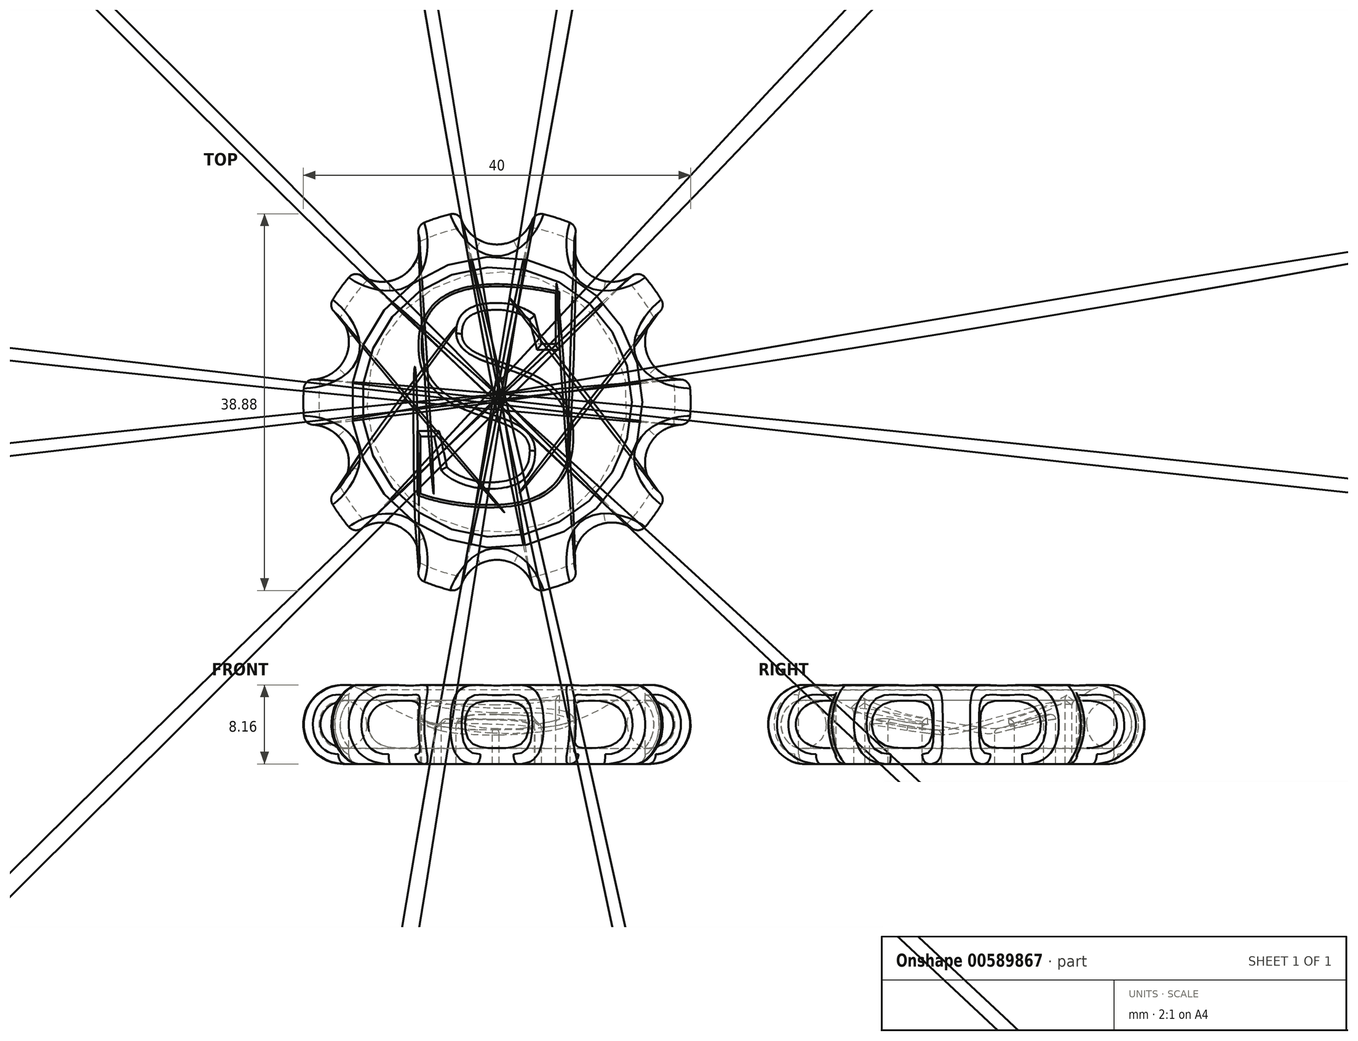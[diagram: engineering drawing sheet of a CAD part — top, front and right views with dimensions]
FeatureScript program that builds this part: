
annotation { "Feature Type Name" : "Feature", "Feature Type Description" : "" }
export const myFeature = defineFeature(function(context is Context, id is Id, definition is map)
    precondition{}
    {
        {
            var Q0;
            Q0=qCreatedBy(makeId("Right.planeOp"),FACE);
            var sketch = newSketch(context, id + "F0", { "sketchPlane" : qUnion([Q0])});
            skArc(sketch, "E0", {"start": v(-13.4, 7.3) * mm, "mid": v(-19.78, 5.4) * mm, "end": v(-15.92, 0) * mm});
            skLineSegment(sketch, "E1", {"start": v(0, 0) * mm, "end": v(-15.92, 0) * mm});
            skLineSegment(sketch, "E2", {"start": v(0, 0) * mm, "end": v(0, 3.46) * mm});
            skFitSpline(sketch, "E3", {"points": [v(0, 3.46) * mm, v(-7.36, 4.25) * mm, v(-13.95, 7.65) * mm], "startDerivative": vector(-15.17, 0.2) * mm, "endDerivative": vector(-12.72, 8.5) * mm});
            skFitSpline(sketch, "E4", {"points": [v(-13.95, 7.65) * mm, v(-15.03, 8.06) * mm], "startDerivative": vector(-1.09, 0.4) * mm, "endDerivative": vector(-1.09, 0.4) * mm});
            skLineSegment(sketch, "E5", {"start": v(0, 3.46) * mm, "end": v(0, 0) * mm});
            skPoint(sketch, "E6.orphan", {"position": v(0, 6.33) * mm});
            skCircle(sketch, "E7", {"center": v(-15.92, 4.08) * mm, "radius": 2.48 * mm});
            skSolve(sketch);
        }
        {
            var Q0;
            {var subQ6=sQuery(id+"F0.wireOp",EDGE,"E1");Q0=makeQuery(id+"F0.imprint","IMPRINT",FACE,{"disambiguationData":[TD([[makeQuery(id+"F0.imprint","IMPRINT",EDGE,{"derivedFrom":subQ6}),-1.0]])]});}
            var Q1;
            Q1=sQuery(id+"F0.wireOp",EDGE,"E5");
            revolve(context, id + "F1", {"entities" : qUnion([Q0]), "axis" : qUnion([Q1]), "revolveType" : RevolveType.FULL});
        }
        {
            var Q0;
            Q0=makeQuery(id+"F0.imprint","IMPRINT",FACE,{"disambiguationData":[TD([[makeQuery(id+"F0.imprint","IMPRINT",EDGE,{"derivedFrom":sQuery(id+"F0.wireOp",EDGE,"E7")}),1.0]])]});
            var Q1;
            Q1=sQuery(id+"F0.wireOp",EDGE,"E5");
            revolve(context, id + "F2", {"entities" : qUnion([Q0]), "axis" : qUnion([Q1]), "revolveType" : RevolveType.FULL});
        }
        {
            var Q0;
            Q0=qCreatedBy(makeId("Top.planeOp"),FACE);
            cPlane(context, id + "F3", {"entities" : qUnion([Q0]), "cplaneType" : CPlaneType.OFFSET, "offset" : 12 * mm, "width" : 150 * mm, "height" : 150 * mm});
        }
        {
            var Q0;
            Q0=qCreatedBy(id+"F3.planeOp",FACE);
            var sketch = newSketch(context, id + "F4", { "sketchPlane" : qUnion([Q0])});
            skText(sketch, "E8", { "text": "S", "fontName": "Tinos-Bold.ttf"});
            const initialGuessF4  = {"E8": [-0.0097, -0.01028, 1, 0, 0.02417]};
            skSetInitialGuess(sketch, initialGuessF4);
            skSolve(sketch);
        }
        {
            var Q0;
            Q0 = qSketchRegion(id + "F4", true);
            extrude(context, id + "F5", {"entities" : qUnion([Q0]), "operationType" : NewBodyOperationType.REMOVE, "oppositeDirection" : true, "depth" : 27.1 * mm, "offsetDistance" : 25 * mm});
        }
        {
            var Q0;
            Q0=qCreatedBy(id+"F3.planeOp",FACE);
            var sketch = newSketch(context, id + "F6", { "sketchPlane" : qUnion([Q0])});
            skCircle(sketch, "E9", {"center": v(0, 20.18) * mm, "radius": 3.9 * mm});
            skCircle(sketch, "E10.1.0", {"center": v(-11.86, 16.33) * mm, "radius": 3.9 * mm});
            skCircle(sketch, "E10.2.0", {"center": v(-19.2, 6.24) * mm, "radius": 3.9 * mm});
            skCircle(sketch, "E10.3.0", {"center": v(-19.2, -6.24) * mm, "radius": 3.9 * mm});
            skCircle(sketch, "E10.4.0", {"center": v(-11.86, -16.33) * mm, "radius": 3.9 * mm});
            skCircle(sketch, "E10.5.0", {"center": v(0, -20.18) * mm, "radius": 3.9 * mm});
            skCircle(sketch, "E10.6.0", {"center": v(11.86, -16.33) * mm, "radius": 3.9 * mm});
            skCircle(sketch, "E10.7.0", {"center": v(19.2, -6.24) * mm, "radius": 3.9 * mm});
            skCircle(sketch, "E10.8.0", {"center": v(19.2, 6.24) * mm, "radius": 3.9 * mm});
            skCircle(sketch, "E10.9.0", {"center": v(11.86, 16.33) * mm, "radius": 3.9 * mm});
            skPoint(sketch, "E10.center", {"position": v(0, 0) * mm});
            skSolve(sketch);
        }
        {
            var Q0;
            Q0 = qSketchRegion(id + "F6", true);
            extrude(context, id + "F7", {"entities" : qUnion([Q0]), "operationType" : NewBodyOperationType.REMOVE, "oppositeDirection" : true, "depth" : 20.8 * mm, "offsetDistance" : 25 * mm});
        }
        {
            var Q0;
            Q0=makeQuery(id+"F7.boolean.opBoolean","INTERSECT",EDGE,{"derivedFrom":[makeQuery(id+"F1.opRevolve","SWEPT_FACE",FACE,{"disambiguationData":[OSD([sQuery(id+"F0.wireOp",EDGE,"E0")])]}),makeQuery(id+"F7.opExtrude","SWEPT_FACE",FACE,{"disambiguationData":[OSD([sQuery(id+"F6.wireOp",EDGE,"E9")])]})]});
            var Q1;
            Q1=makeQuery(id+"F7.boolean.opBoolean","INTERSECT",EDGE,{"derivedFrom":[makeQuery(id+"F1.opRevolve","SWEPT_FACE",FACE,{"disambiguationData":[OSD([sQuery(id+"F0.wireOp",EDGE,"E0")])]}),makeQuery(id+"F7.opExtrude","SWEPT_FACE",FACE,{"disambiguationData":[OSD([sQuery(id+"F6.wireOp",EDGE,"E10.8.0")])]})]});
            var Q2;
            Q2=makeQuery(id+"F7.boolean.opBoolean","INTERSECT",EDGE,{"derivedFrom":[makeQuery(id+"F1.opRevolve","SWEPT_FACE",FACE,{"disambiguationData":[OSD([sQuery(id+"F0.wireOp",EDGE,"E0")])]}),makeQuery(id+"F7.opExtrude","SWEPT_FACE",FACE,{"disambiguationData":[OSD([sQuery(id+"F6.wireOp",EDGE,"E10.9.0")])]})]});
            var Q3;
            Q3=makeQuery(id+"F7.boolean.opBoolean","INTERSECT",EDGE,{"derivedFrom":[makeQuery(id+"F1.opRevolve","SWEPT_FACE",FACE,{"disambiguationData":[OSD([sQuery(id+"F0.wireOp",EDGE,"E0")])]}),makeQuery(id+"F7.opExtrude","SWEPT_FACE",FACE,{"disambiguationData":[OSD([sQuery(id+"F6.wireOp",EDGE,"E10.7.0")])]})]});
            var Q4;
            Q4=makeQuery(id+"F7.boolean.opBoolean","INTERSECT",EDGE,{"derivedFrom":[makeQuery(id+"F1.opRevolve","SWEPT_FACE",FACE,{"disambiguationData":[OSD([sQuery(id+"F0.wireOp",EDGE,"E0")])]}),makeQuery(id+"F7.opExtrude","SWEPT_FACE",FACE,{"disambiguationData":[OSD([sQuery(id+"F6.wireOp",EDGE,"E10.6.0")])]})]});
            var Q5;
            Q5=makeQuery(id+"F7.boolean.opBoolean","INTERSECT",EDGE,{"derivedFrom":[makeQuery(id+"F1.opRevolve","SWEPT_FACE",FACE,{"disambiguationData":[OSD([sQuery(id+"F0.wireOp",EDGE,"E0")])]}),makeQuery(id+"F7.opExtrude","SWEPT_FACE",FACE,{"disambiguationData":[OSD([sQuery(id+"F6.wireOp",EDGE,"E10.5.0")])]})]});
            var Q6;
            Q6=makeQuery(id+"F7.boolean.opBoolean","INTERSECT",EDGE,{"derivedFrom":[makeQuery(id+"F1.opRevolve","SWEPT_FACE",FACE,{"disambiguationData":[OSD([sQuery(id+"F0.wireOp",EDGE,"E0")])]}),makeQuery(id+"F7.opExtrude","SWEPT_FACE",FACE,{"disambiguationData":[OSD([sQuery(id+"F6.wireOp",EDGE,"E10.4.0")])]})]});
            var Q7;
            Q7=makeQuery(id+"F7.boolean.opBoolean","INTERSECT",EDGE,{"derivedFrom":[makeQuery(id+"F1.opRevolve","SWEPT_FACE",FACE,{"disambiguationData":[OSD([sQuery(id+"F0.wireOp",EDGE,"E0")])]}),makeQuery(id+"F7.opExtrude","SWEPT_FACE",FACE,{"disambiguationData":[OSD([sQuery(id+"F6.wireOp",EDGE,"E10.3.0")])]})]});
            var Q8;
            Q8=makeQuery(id+"F7.boolean.opBoolean","INTERSECT",EDGE,{"derivedFrom":[makeQuery(id+"F1.opRevolve","SWEPT_FACE",FACE,{"disambiguationData":[OSD([sQuery(id+"F0.wireOp",EDGE,"E0")])]}),makeQuery(id+"F7.opExtrude","SWEPT_FACE",FACE,{"disambiguationData":[OSD([sQuery(id+"F6.wireOp",EDGE,"E10.2.0")])]})]});
            var Q9;
            Q9=makeQuery(id+"F7.boolean.opBoolean","INTERSECT",EDGE,{"derivedFrom":[makeQuery(id+"F1.opRevolve","SWEPT_FACE",FACE,{"disambiguationData":[OSD([sQuery(id+"F0.wireOp",EDGE,"E0")])]}),makeQuery(id+"F7.opExtrude","SWEPT_FACE",FACE,{"disambiguationData":[OSD([sQuery(id+"F6.wireOp",EDGE,"E10.1.0")])]})]});
            fillet(context, id + "F8", {"entities" : qUnion([Q0, Q1, Q2, Q3, Q4, Q5, Q6, Q7, Q8, Q9]), "radius" : 1 * mm, "tangentPropagation" : true, "allowEdgeOverflow" : false});
        }
        {
            var Q0;
            Q0=makeQuery(id+"F5.boolean.opBoolean","INTERSECT",EDGE,{"derivedFrom":[makeQuery(id+"F1.opRevolve","SWEPT_FACE",FACE,{"disambiguationData":[OSD([sQuery(id+"F0.wireOp",EDGE,"E3")])]}),makeQuery(id+"F5.opExtrude","SWEPT_FACE",FACE,{"disambiguationData":[OSD([sQuery(id+"F4.wireOp",EDGE,"E8.sketch_text.stroke-27")])]})]});
            var Q1;
            Q1=makeQuery(id+"F5.boolean.opBoolean","INTERSECT",EDGE,{"derivedFrom":[makeQuery(id+"F1.opRevolve","SWEPT_FACE",FACE,{"disambiguationData":[OSD([sQuery(id+"F0.wireOp",EDGE,"E3")])]}),makeQuery(id+"F5.opExtrude","SWEPT_FACE",FACE,{"disambiguationData":[OSD([sQuery(id+"F4.wireOp",EDGE,"E8.sketch_text.stroke-26")])]})]});
            var Q2;
            Q2=makeQuery(id+"F5.boolean.opBoolean","INTERSECT",EDGE,{"derivedFrom":[makeQuery(id+"F1.opRevolve","SWEPT_FACE",FACE,{"disambiguationData":[OSD([sQuery(id+"F0.wireOp",EDGE,"E3")])]}),makeQuery(id+"F5.opExtrude","SWEPT_FACE",FACE,{"disambiguationData":[OSD([sQuery(id+"F4.wireOp",EDGE,"E8.sketch_text.stroke-25")])]})]});
            var Q3;
            Q3=makeQuery(id+"F5.boolean.opBoolean","INTERSECT",EDGE,{"derivedFrom":[makeQuery(id+"F1.opRevolve","SWEPT_FACE",FACE,{"disambiguationData":[OSD([sQuery(id+"F0.wireOp",EDGE,"E3")])]}),makeQuery(id+"F5.opExtrude","SWEPT_FACE",FACE,{"disambiguationData":[OSD([sQuery(id+"F4.wireOp",EDGE,"E8.sketch_text.stroke-24")])]})]});
            var Q4;
            Q4=makeQuery(id+"F5.boolean.opBoolean","INTERSECT",EDGE,{"derivedFrom":[makeQuery(id+"F1.opRevolve","SWEPT_FACE",FACE,{"disambiguationData":[OSD([sQuery(id+"F0.wireOp",EDGE,"E3")])]}),makeQuery(id+"F5.opExtrude","SWEPT_FACE",FACE,{"disambiguationData":[OSD([sQuery(id+"F4.wireOp",EDGE,"E8.sketch_text.stroke-23")])]})]});
            var Q5;
            Q5=makeQuery(id+"F5.boolean.opBoolean","INTERSECT",EDGE,{"derivedFrom":[makeQuery(id+"F1.opRevolve","SWEPT_FACE",FACE,{"disambiguationData":[OSD([sQuery(id+"F0.wireOp",EDGE,"E3")])]}),makeQuery(id+"F5.opExtrude","SWEPT_FACE",FACE,{"disambiguationData":[OSD([sQuery(id+"F4.wireOp",EDGE,"E8.sketch_text.stroke-22")])]})]});
            var Q6;
            Q6=makeQuery(id+"F5.boolean.opBoolean","INTERSECT",EDGE,{"derivedFrom":[makeQuery(id+"F1.opRevolve","SWEPT_FACE",FACE,{"disambiguationData":[OSD([sQuery(id+"F0.wireOp",EDGE,"E3")])]}),makeQuery(id+"F5.opExtrude","SWEPT_FACE",FACE,{"disambiguationData":[OSD([sQuery(id+"F4.wireOp",EDGE,"E8.sketch_text.stroke-21")])]})]});
            var Q7;
            Q7=makeQuery(id+"F5.boolean.opBoolean","INTERSECT",EDGE,{"derivedFrom":[makeQuery(id+"F1.opRevolve","SWEPT_FACE",FACE,{"disambiguationData":[OSD([sQuery(id+"F0.wireOp",EDGE,"E3")])]}),makeQuery(id+"F5.opExtrude","SWEPT_FACE",FACE,{"disambiguationData":[OSD([sQuery(id+"F4.wireOp",EDGE,"E8.sketch_text.stroke-20")])]})]});
            var Q8;
            Q8=makeQuery(id+"F5.boolean.opBoolean","INTERSECT",EDGE,{"derivedFrom":[makeQuery(id+"F1.opRevolve","SWEPT_FACE",FACE,{"disambiguationData":[OSD([sQuery(id+"F0.wireOp",EDGE,"E3")])]}),makeQuery(id+"F5.opExtrude","SWEPT_FACE",FACE,{"disambiguationData":[OSD([sQuery(id+"F4.wireOp",EDGE,"E8.sketch_text.stroke-19")])]})]});
            var Q9;
            Q9=makeQuery(id+"F5.boolean.opBoolean","INTERSECT",EDGE,{"derivedFrom":[makeQuery(id+"F1.opRevolve","SWEPT_FACE",FACE,{"disambiguationData":[OSD([sQuery(id+"F0.wireOp",EDGE,"E3")])]}),makeQuery(id+"F5.opExtrude","SWEPT_FACE",FACE,{"disambiguationData":[OSD([sQuery(id+"F4.wireOp",EDGE,"E8.sketch_text.stroke-18")])]})]});
            var Q10;
            Q10=makeQuery(id+"F5.boolean.opBoolean","INTERSECT",EDGE,{"derivedFrom":[makeQuery(id+"F1.opRevolve","SWEPT_FACE",FACE,{"disambiguationData":[OSD([sQuery(id+"F0.wireOp",EDGE,"E3")])]}),makeQuery(id+"F5.opExtrude","SWEPT_FACE",FACE,{"disambiguationData":[OSD([sQuery(id+"F4.wireOp",EDGE,"E8.sketch_text.stroke-17")])]})]});
            var Q11;
            Q11=makeQuery(id+"F5.boolean.opBoolean","INTERSECT",EDGE,{"derivedFrom":[makeQuery(id+"F1.opRevolve","SWEPT_FACE",FACE,{"disambiguationData":[OSD([sQuery(id+"F0.wireOp",EDGE,"E3")])]}),makeQuery(id+"F5.opExtrude","SWEPT_FACE",FACE,{"disambiguationData":[OSD([sQuery(id+"F4.wireOp",EDGE,"E8.sketch_text.stroke-16")])]})]});
            var Q12;
            Q12=makeQuery(id+"F5.boolean.opBoolean","INTERSECT",EDGE,{"derivedFrom":[makeQuery(id+"F1.opRevolve","SWEPT_FACE",FACE,{"disambiguationData":[OSD([sQuery(id+"F0.wireOp",EDGE,"E3")])]}),makeQuery(id+"F5.opExtrude","SWEPT_FACE",FACE,{"disambiguationData":[OSD([sQuery(id+"F4.wireOp",EDGE,"E8.sketch_text.stroke-14")])]})]});
            var Q13;
            Q13=makeQuery(id+"F5.boolean.opBoolean","INTERSECT",EDGE,{"derivedFrom":[makeQuery(id+"F1.opRevolve","SWEPT_FACE",FACE,{"disambiguationData":[OSD([sQuery(id+"F0.wireOp",EDGE,"E3")])]}),makeQuery(id+"F5.opExtrude","SWEPT_FACE",FACE,{"disambiguationData":[OSD([sQuery(id+"F4.wireOp",EDGE,"E8.sketch_text.stroke-15")])]})]});
            var Q14;
            Q14=makeQuery(id+"F5.boolean.opBoolean","INTERSECT",EDGE,{"derivedFrom":[makeQuery(id+"F1.opRevolve","SWEPT_FACE",FACE,{"disambiguationData":[OSD([sQuery(id+"F0.wireOp",EDGE,"E3")])]}),makeQuery(id+"F5.opExtrude","SWEPT_FACE",FACE,{"disambiguationData":[OSD([sQuery(id+"F4.wireOp",EDGE,"E8.sketch_text.stroke-13")])]})]});
            var Q15;
            Q15=makeQuery(id+"F5.boolean.opBoolean","INTERSECT",EDGE,{"derivedFrom":[makeQuery(id+"F1.opRevolve","SWEPT_FACE",FACE,{"disambiguationData":[OSD([sQuery(id+"F0.wireOp",EDGE,"E3")])]}),makeQuery(id+"F5.opExtrude","SWEPT_FACE",FACE,{"disambiguationData":[OSD([sQuery(id+"F4.wireOp",EDGE,"E8.sketch_text.stroke-12")])]})]});
            var Q16;
            Q16=makeQuery(id+"F5.boolean.opBoolean","INTERSECT",EDGE,{"derivedFrom":[makeQuery(id+"F1.opRevolve","SWEPT_FACE",FACE,{"disambiguationData":[OSD([sQuery(id+"F0.wireOp",EDGE,"E3")])]}),makeQuery(id+"F5.opExtrude","SWEPT_FACE",FACE,{"disambiguationData":[OSD([sQuery(id+"F4.wireOp",EDGE,"E8.sketch_text.stroke-11")])]})]});
            var Q17;
            Q17=makeQuery(id+"F5.boolean.opBoolean","INTERSECT",EDGE,{"derivedFrom":[makeQuery(id+"F1.opRevolve","SWEPT_FACE",FACE,{"disambiguationData":[OSD([sQuery(id+"F0.wireOp",EDGE,"E3")])]}),makeQuery(id+"F5.opExtrude","SWEPT_FACE",FACE,{"disambiguationData":[OSD([sQuery(id+"F4.wireOp",EDGE,"E8.sketch_text.stroke-9")])]})]});
            var Q18;
            Q18=makeQuery(id+"F5.boolean.opBoolean","INTERSECT",EDGE,{"derivedFrom":[makeQuery(id+"F1.opRevolve","SWEPT_FACE",FACE,{"disambiguationData":[OSD([sQuery(id+"F0.wireOp",EDGE,"E3")])]}),makeQuery(id+"F5.opExtrude","SWEPT_FACE",FACE,{"disambiguationData":[OSD([sQuery(id+"F4.wireOp",EDGE,"E8.sketch_text.stroke-10")])]})]});
            var Q19;
            Q19=makeQuery(id+"F5.boolean.opBoolean","INTERSECT",EDGE,{"derivedFrom":[makeQuery(id+"F1.opRevolve","SWEPT_FACE",FACE,{"disambiguationData":[OSD([sQuery(id+"F0.wireOp",EDGE,"E3")])]}),makeQuery(id+"F5.opExtrude","SWEPT_FACE",FACE,{"disambiguationData":[OSD([sQuery(id+"F4.wireOp",EDGE,"E8.sketch_text.stroke-8")])]})]});
            var Q20;
            Q20=makeQuery(id+"F5.boolean.opBoolean","INTERSECT",EDGE,{"derivedFrom":[makeQuery(id+"F1.opRevolve","SWEPT_FACE",FACE,{"disambiguationData":[OSD([sQuery(id+"F0.wireOp",EDGE,"E3")])]}),makeQuery(id+"F5.opExtrude","SWEPT_FACE",FACE,{"disambiguationData":[OSD([sQuery(id+"F4.wireOp",EDGE,"E8.sketch_text.stroke-7")])]})]});
            var Q21;
            Q21=makeQuery(id+"F5.boolean.opBoolean","INTERSECT",EDGE,{"derivedFrom":[makeQuery(id+"F1.opRevolve","SWEPT_FACE",FACE,{"disambiguationData":[OSD([sQuery(id+"F0.wireOp",EDGE,"E3")])]}),makeQuery(id+"F5.opExtrude","SWEPT_FACE",FACE,{"disambiguationData":[OSD([sQuery(id+"F4.wireOp",EDGE,"E8.sketch_text.stroke-6")])]})]});
            var Q22;
            Q22=makeQuery(id+"F5.boolean.opBoolean","INTERSECT",EDGE,{"derivedFrom":[makeQuery(id+"F1.opRevolve","SWEPT_FACE",FACE,{"disambiguationData":[OSD([sQuery(id+"F0.wireOp",EDGE,"E3")])]}),makeQuery(id+"F5.opExtrude","SWEPT_FACE",FACE,{"disambiguationData":[OSD([sQuery(id+"F4.wireOp",EDGE,"E8.sketch_text.stroke-5")])]})]});
            var Q23;
            Q23=makeQuery(id+"F5.boolean.opBoolean","INTERSECT",EDGE,{"derivedFrom":[makeQuery(id+"F1.opRevolve","SWEPT_FACE",FACE,{"disambiguationData":[OSD([sQuery(id+"F0.wireOp",EDGE,"E3")])]}),makeQuery(id+"F5.opExtrude","SWEPT_FACE",FACE,{"disambiguationData":[OSD([sQuery(id+"F4.wireOp",EDGE,"E8.sketch_text.stroke-4")])]})]});
            var Q24;
            Q24=makeQuery(id+"F5.boolean.opBoolean","INTERSECT",EDGE,{"derivedFrom":[makeQuery(id+"F1.opRevolve","SWEPT_FACE",FACE,{"disambiguationData":[OSD([sQuery(id+"F0.wireOp",EDGE,"E3")])]}),makeQuery(id+"F5.opExtrude","SWEPT_FACE",FACE,{"disambiguationData":[OSD([sQuery(id+"F4.wireOp",EDGE,"E8.sketch_text.stroke-3")])]})]});
            var Q25;
            Q25=makeQuery(id+"F5.boolean.opBoolean","INTERSECT",EDGE,{"derivedFrom":[makeQuery(id+"F1.opRevolve","SWEPT_FACE",FACE,{"disambiguationData":[OSD([sQuery(id+"F0.wireOp",EDGE,"E3")])]}),makeQuery(id+"F5.opExtrude","SWEPT_FACE",FACE,{"disambiguationData":[OSD([sQuery(id+"F4.wireOp",EDGE,"E8.sketch_text.stroke-28")])]})]});
            var Q26;
            Q26=makeQuery(id+"F5.boolean.opBoolean","INTERSECT",EDGE,{"derivedFrom":[makeQuery(id+"F1.opRevolve","SWEPT_FACE",FACE,{"disambiguationData":[OSD([sQuery(id+"F0.wireOp",EDGE,"E3")])]}),makeQuery(id+"F5.opExtrude","SWEPT_FACE",FACE,{"disambiguationData":[OSD([sQuery(id+"F4.wireOp",EDGE,"E8.sketch_text.stroke-1")])]})]});
            var Q27;
            Q27=makeQuery(id+"F5.boolean.opBoolean","INTERSECT",EDGE,{"derivedFrom":[makeQuery(id+"F1.opRevolve","SWEPT_FACE",FACE,{"disambiguationData":[OSD([sQuery(id+"F0.wireOp",EDGE,"E3")])]}),makeQuery(id+"F5.opExtrude","SWEPT_FACE",FACE,{"disambiguationData":[OSD([sQuery(id+"F4.wireOp",EDGE,"E8.sketch_text.stroke-2")])]})]});
            var Q28;
            Q28=makeQuery(id+"F5.boolean.opBoolean","INTERSECT",EDGE,{"derivedFrom":[makeQuery(id+"F1.opRevolve","SWEPT_FACE",FACE,{"disambiguationData":[OSD([sQuery(id+"F0.wireOp",EDGE,"E3")])]}),makeQuery(id+"F5.opExtrude","SWEPT_FACE",FACE,{"disambiguationData":[OSD([sQuery(id+"F4.wireOp",EDGE,"E8.sketch_text.stroke-0")])]})]});
            fillet(context, id + "F9", {"entities" : qUnion([Q0, Q1, Q2, Q3, Q4, Q5, Q6, Q7, Q8, Q9, Q10, Q11, Q12, Q13, Q14, Q15, Q16, Q17, Q18, Q19, Q20, Q21, Q22, Q23, Q24, Q25, Q26, Q27, Q28]), "radius" : .5 * mm, "tangentPropagation" : true, "allowEdgeOverflow" : false});
        }
    });
